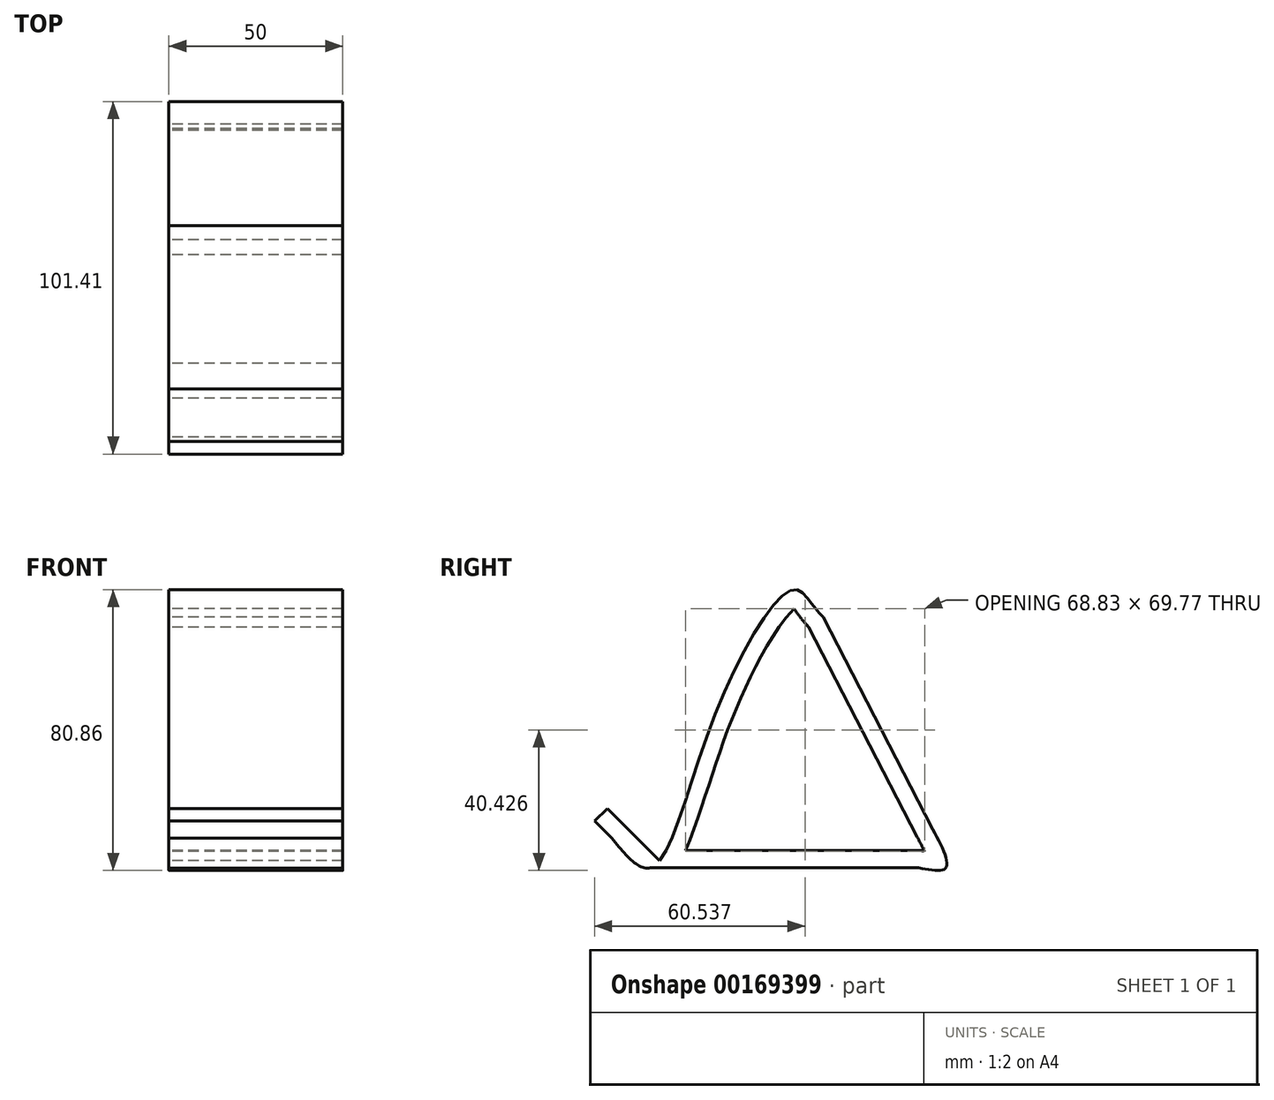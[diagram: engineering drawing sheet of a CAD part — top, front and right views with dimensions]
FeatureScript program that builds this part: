
annotation { "Feature Type Name" : "Feature", "Feature Type Description" : "" }
export const myFeature = defineFeature(function(context is Context, id is Id, definition is map)
    precondition{}
    {
        {
            var Q0;
            Q0=qCreatedBy(makeId("Right.planeOp"),FACE);
            var sketch = newSketch(context, id + "F0", { "sketchPlane" : qUnion([Q0])});
            skLineSegment(sketch, "E0", {"start": v(-41.5, -36.38) * mm, "end": v(35.65, -36.38) * mm});
            skFitSpline(sketch, "E1", {"points": [v(35.65, -36.38) * mm, v(43.54, -36.38) * mm, v(39.74, -25.28) * mm], "startDerivative": vector(23.01, -4.55) * mm, "endDerivative": vector(-13.62, 25.76) * mm});
            skLineSegment(sketch, "E2", {"start": v(39.74, -25.28) * mm, "end": v(8.18, 35.8) * mm});
            skFitSpline(sketch, "E3", {"points": [v(8.18, 35.8) * mm, v(4.97, 39.6) * mm, v(0, 43.69) * mm, v(-23.67, 5.7) * mm, v(-41.5, -36.38) * mm, v(-52.6, -27.9) * mm], "startDerivative": vector(-30.38, 32.65) * mm, "endDerivative": vector(-68.38, 83.62) * mm});
            skLineSegment(sketch, "E4", {"start": v(-52.6, -27.9) * mm, "end": v(-57.56, -22.94) * mm});
            skLineSegment(sketch, "E5", {"start": v(-57.56, -22.94) * mm, "end": v(-53.91, -19.29) * mm});
            skLineSegment(sketch, "E6", {"start": v(-53.91, -19.29) * mm, "end": v(-38.86, -34.34) * mm});
            skSolve(sketch);
        }
        {
            var Q0;
            {var subQ3=sQuery(id+"F0.wireOp",EDGE,"E0");Q0=makeQuery(id+"F0.imprint","IMPRINT",FACE,{"disambiguationData":[TD([[makeQuery(id+"F0.imprint","IMPRINT",EDGE,{"derivedFrom":subQ3}),1.0]])]});}
            var Q1;
            {var subQ0=sQuery(id+"F0.wireOp",EDGE,"E4");Q1=makeQuery(id+"F0.imprint","IMPRINT",FACE,{"disambiguationData":[TD([[makeQuery(id+"F0.imprint","IMPRINT",EDGE,{"derivedFrom":subQ0}),-1.0]])]});}
            extrude(context, id + "F1", {"entities" : qUnion([Q0, Q1]), "depth" : 50 * mm});
        }
        {
            var Q0;
            Q0=makeQuery(id+"F1.opExtrude","CAP_FACE",FACE,{"disambiguationData":[OSD([sQuery(id+"F0.wireOp",EDGE,"E0"),sQuery(id+"F0.wireOp",EDGE,"E1"),sQuery(id+"F0.wireOp",EDGE,"E2"),sQuery(id+"F0.wireOp",EDGE,"E3"),sQuery(id+"F0.wireOp",EDGE,"E4"),sQuery(id+"F0.wireOp",EDGE,"E5"),sQuery(id+"F0.wireOp",EDGE,"E6")])],"isStart":false});
            var Q1;
            Q1=makeQuery(id+"F1.opExtrude","CAP_FACE",FACE,{"disambiguationData":[OSD([sQuery(id+"F0.wireOp",EDGE,"E0"),sQuery(id+"F0.wireOp",EDGE,"E1"),sQuery(id+"F0.wireOp",EDGE,"E2"),sQuery(id+"F0.wireOp",EDGE,"E3"),sQuery(id+"F0.wireOp",EDGE,"E4"),sQuery(id+"F0.wireOp",EDGE,"E5"),sQuery(id+"F0.wireOp",EDGE,"E6")])],"isStart":true});
            shell(context, id + "F2", {"entities" : qUnion([Q0, Q1]), "thickness" : 5 * mm});
        }
    });
